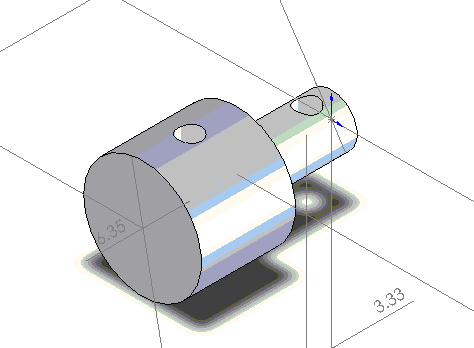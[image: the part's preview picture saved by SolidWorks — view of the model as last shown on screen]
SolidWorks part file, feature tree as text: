
SOLIDWORKS PART (.sldprt)
format: sldprt  version: not decoded by parser v0  size: 164,352 bytes
history: native  units: mm
features: sketch x4, cut_extrude x3, material x1, extrude x1 + 1 further entry (+14 scaffold rows collapsed)
feature tree (24):
  scaffold x14  (default folders/planes/origin — collapsed)
  material  "Material <not specified>"
  "Annotations"  RD1=15.85mm RD2=25.4mm RD3=12.75mm RD4=6.96mm RD5=3.325mm RD6=6.35mm
  sketch  "Sketch1"  dims[D1=~4.59375mm]
  extrude  "Extrude1"  Depth=25.4mm
  sketch  "Sketch2"  dims[D1=3.175mm]
  cut_extrude  "Cut-Extrude1"  Depth=12.75mm
  sketch  "Sketch3"  dims[D1=~1.621674mm]
  cut_extrude  "Cut-Extrude2"  [1 undecoded]
  sketch  "Sketch4"  dims[D1=3.1mm D2=15.725mm]
  cut_extrude  "Cut-Extrude3"  [1 undecoded]
decode coverage: 6 of 8 modeling features carry decoded parameters; 1 rows unclassified (native names shown)
note: ~ marks probable driven/reference dimensions
note: 2 parameter values undecoded
note: suppression state not decoded; provenance and decode notes live in map.json
